# Revit family: VISS SQUARE LED LIGHT
name_source: partatom
category: Lighting Fixtures
units: mm (PartAtom-declared; Revit-internal decimal feet)

## family parameters
Cut with Voids When Loaded = No
Host = Face
Light Source = Yes
Part Type = Normal
Room Calculation Point = No
Round Connector Dimension = Use Diameter
Shared = No

## types (64) — shared parameters
Acoustic = Acoustic -130
Average life based on 77F(HRS) = 50000
B = 0' - 3 1/2"
CRI = 90
Color Filter = 16777215
Default Elevation = 0' - 0"
Description = The Viss Series has an unique square and round style with an LED light source illuminating its inner surface.
Dimming / Control = 0-10V
Dimming Lamp Color Temperature Shift = <None>
Fixture Height = 4' - 11"
IP Rating = 20
Load Classification = Lighting
Manufacturer = Above All Lighting
Power Factor = 1
Tilt Angle = -90.00°
Type Comments = VISS SQUARE LED LIGHT
URL = https://www.abovealllighting.com
Voltage = 120-277 V

## per-type parameters (varying)
| type | Acoustic Body | Aircraft Cable Pendant Mount | Apparent Load | B1 | B2 | Finish/Color | Fixture Width | H1 | Order number | Photometric Web File | Surface Acoustic Body | Surface Mount | Wattage Comments |
| VSI-S-1514-30901-ACPMK-WH | No | Yes | 19 VA | 0' - 6 19/32" | 0' - 3 3/32" | White | 1' - 2 3/16" | 4' - 11 3/32" | 17486 | generic | No | No | 15 W |
| VSI-S-2518-30901-ACPMK-WH | No | Yes | 31 VA | 0' - 8 11/32" | 0' - 4 27/32" | White | 1' - 5 11/16" | 4' - 11 3/16" | 17487 | generic | No | No | 25 W |
| VSI-S-3624-30901-ACPMK-WH | No | Yes | 31 VA | 0' - 11 5/16" | 0' - 7 13/16" | White | 1' - 11 19/32" | 4' - 11 1/2" | 17488 | generic | No | No | 36 W |
| VSI-S-5032-30901-ACPMK-WH | No | Yes | 63 VA | 1' - 3 1/4" | 0' - 11 3/4" | White | 2' - 7 1/2" | 5' - 0 5/32" | 17489 | generic | No | No | 50 W |
| VSI-S-1514-30901-ACPMK-BK | No | Yes | 19 VA | 0' - 6 19/32" | 0' - 3 3/32" | Black | 1' - 2 3/16" | 4' - 11 3/32" | 17490 | generic | No | No | 15 W |
| VSI-S-2518-30901-ACPMK-BK | No | Yes | 31 VA | 0' - 8 11/32" | 0' - 4 27/32" | Black | 1' - 5 11/16" | 4' - 11 3/16" | 17491 | generic | No | No | 25 W |
| VSI-S-3624-30901-ACPMK-BK | No | Yes | 31 VA | 0' - 11 5/16" | 0' - 7 13/16" | Black | 1' - 11 19/32" | 4' - 11 1/2" | 17492 | generic | No | No | 36 W |
| VSI-S-5032-30901-ACPMK-BK | No | Yes | 63 VA | 1' - 3 1/4" | 0' - 11 3/4" | Black | 2' - 7 1/2" | 5' - 0 5/32" | 17493 | generic | No | No | 50 W |
| VSI-S-1514-40901-ACPMK-WH | No | Yes | 19 VA | 0' - 6 19/32" | 0' - 3 3/32" | White | 1' - 2 3/16" | 4' - 11 3/32" | 17494 | generic | No | No | 15 W |
| VSI-S-2518-40901-ACPMK-WH | No | Yes | 31 VA | 0' - 8 11/32" | 0' - 4 27/32" | White | 1' - 5 11/16" | 4' - 11 3/16" | 17495 | generic | No | No | 25 W |
| VSI-S-3624-40901-ACPMK-WH | No | Yes | 31 VA | 0' - 11 5/16" | 0' - 7 13/16" | White | 1' - 11 19/32" | 4' - 11 1/2" | 17496 | VSI-S-3624-40901.IES | No | No | 36 W |
| VSI-S-5032-40901-ACPMK-WH | No | Yes | 63 VA | 1' - 3 1/4" | 0' - 11 3/4" | White | 2' - 7 1/2" | 5' - 0 5/32" | 17497 | VSI-S-5032-40901.IES | No | No | 50 W |
| VSI-S-1514-40901-ACPMK-BK | No | Yes | 19 VA | 0' - 6 19/32" | 0' - 3 3/32" | Black | 1' - 2 3/16" | 4' - 11 3/32" | 17498 | generic | No | No | 15 W |
| VSI-S-2518-40901-ACPMK-BK | No | Yes | 31 VA | 0' - 8 11/32" | 0' - 4 27/32" | Black | 1' - 5 11/16" | 4' - 11 3/16" | 17499 | generic | No | No | 25 W |
| VSI-S-3624-40901-ACPMK-BK | No | Yes | 31 VA | 0' - 11 5/16" | 0' - 7 13/16" | Black | 1' - 11 19/32" | 4' - 11 1/2" | 17500 | VSI-S-3624-40901.IES | No | No | 36 W |
| VSI-S-5032-40901-ACPMK-BK | No | Yes | 63 VA | 1' - 3 1/4" | 0' - 11 3/4" | Black | 2' - 7 1/2" | 5' - 0 5/32" | 17501 | VSI-S-5032-40901.IES | No | No | 50 W |
| VSI-S-LA-1514-30901-ACPMK-WH-NSAC-021 130 | Yes | Yes | 19 VA | 0' - 6 19/32" | 0' - 3 3/32" | White | 1' - 2 3/16" | 4' - 11 3/32" | 17502 | generic | No | No | 15 W |
| VSI-S-LA-2518-30901-ACPMK-WH-NSAC-021 130 | Yes | Yes | 31 VA | 0' - 8 11/32" | 0' - 4 27/32" | White | 1' - 5 11/16" | 4' - 11 3/16" | 17503 | generic | No | No | 25 W |
| VSI-S-LA-3624-30901-ACPMK-WH-NSAC-021 130 | Yes | Yes | 31 VA | 0' - 11 5/16" | 0' - 7 13/16" | White | 1' - 11 19/32" | 4' - 11 1/2" | 17504 | generic | No | No | 36 W |
| VSI-S-LA-5032-30901-ACPMK-WH-NSAC-021 130 | Yes | Yes | 63 VA | 1' - 3 1/4" | 0' - 11 3/4" | White | 2' - 7 1/2" | 5' - 0 5/32" | 17505 | generic | No | No | 50 W |
| VSI-S-LA-1514-30901-ACPMK-BK-NSAC-021 130 | Yes | Yes | 19 VA | 0' - 6 19/32" | 0' - 3 3/32" | Black | 1' - 2 3/16" | 4' - 11 3/32" | 17506 | generic | No | No | 15 W |
| VSI-S-LA-2518-30901-ACPMK-BK-NSAC-021 130 | Yes | Yes | 31 VA | 0' - 8 11/32" | 0' - 4 27/32" | Black | 1' - 5 11/16" | 4' - 11 3/16" | 17507 | generic | No | No | 25 W |
| VSI-S-LA-3624-30901-ACPMK-BK-NSAC-021 130 | Yes | Yes | 31 VA | 0' - 11 5/16" | 0' - 7 13/16" | Black | 1' - 11 19/32" | 4' - 11 1/2" | 17508 | generic | No | No | 36 W |
| VSI-S-LA-5032-30901-ACPMK-BK-NSAC-021 130 | Yes | Yes | 63 VA | 1' - 3 1/4" | 0' - 11 3/4" | Black | 2' - 7 1/2" | 5' - 0 5/32" | 17509 | generic | No | No | 50 W |
| VSI-S-LA-1514-40901-ACPMK-WH-NSAC-021 130 | Yes | Yes | 19 VA | 0' - 6 19/32" | 0' - 3 3/32" | White | 1' - 2 3/16" | 4' - 11 3/32" | 17510 | generic | No | No | 15 W |
| VSI-S-LA-2518-40901-ACPMK-WH-NSAC-021 130 | Yes | Yes | 31 VA | 0' - 8 11/32" | 0' - 4 27/32" | White | 1' - 5 11/16" | 4' - 11 3/16" | 17511 | generic | No | No | 25 W |
| VSI-S-LA-3624-40901-ACPMK-WH-NSAC-021 130 | Yes | Yes | 31 VA | 0' - 11 5/16" | 0' - 7 13/16" | White | 1' - 11 19/32" | 4' - 11 1/2" | 17512 | generic | No | No | 36 W |
| VSI-S-LA-5032-40901-ACPMK-WH-NSAC-021 130 | Yes | Yes | 63 VA | 1' - 3 1/4" | 0' - 11 3/4" | White | 2' - 7 1/2" | 5' - 0 5/32" | 17513 | generic | No | No | 50 W |
| VSI-S-LA-1514-40901-ACPMK-BK-NSAC-021 130 | Yes | Yes | 19 VA | 0' - 6 19/32" | 0' - 3 3/32" | Black | 1' - 2 3/16" | 4' - 11 3/32" | 17514 | generic | No | No | 15 W |
| VSI-S-LA-2518-40901-ACPMK-BK-NSAC-021 130 | Yes | Yes | 31 VA | 0' - 8 11/32" | 0' - 4 27/32" | Black | 1' - 5 11/16" | 4' - 11 3/16" | 17515 | generic | No | No | 25 W |
| VSI-S-LA-3624-40901-ACPMK-BK-NSAC-021 130 | Yes | Yes | 31 VA | 0' - 11 5/16" | 0' - 7 13/16" | Black | 1' - 11 19/32" | 4' - 11 1/2" | 17516 | generic | No | No | 36 W |
| VSI-S-LA-5032-40901-ACPMK-BK-NSAC-021 130 | Yes | Yes | 63 VA | 1' - 3 1/4" | 0' - 11 3/4" | Black | 2' - 7 1/2" | 5' - 0 5/32" | 17517 | generic | No | No | 50 W |
| VSI-S-1514-30901-SMK-WH | No | No | 19 VA | 0' - 6 19/32" | 0' - 3 3/32" | White | 1' - 2 3/16" | 4' - 11 3/32" | 17625 | generic | No | Yes | 15 W |
| VSI-S-2518-30901-SMK-WH | No | No | 31 VA | 0' - 8 11/32" | 0' - 4 27/32" | White | 1' - 5 11/16" | 4' - 11 3/16" | 17626 | generic | No | Yes | 25 W |
| VSI-S-3624-30901-SMK-WH | No | No | 31 VA | 0' - 11 5/16" | 0' - 7 13/16" | White | 1' - 11 19/32" | 4' - 11 1/2" | 17627 | generic | No | Yes | 36 W |
| VSI-S-5032-30901-SMK-WH | No | No | 63 VA | 1' - 3 1/4" | 0' - 11 3/4" | White | 2' - 7 1/2" | 5' - 0 5/32" | 17628 | generic | No | Yes | 50 W |
| VSI-S-1514-30901-SMK-BK | No | No | 19 VA | 0' - 6 19/32" | 0' - 3 3/32" | Black | 1' - 2 3/16" | 4' - 11 3/32" | 17629 | generic | No | Yes | 15 W |
| VSI-S-2518-30901-SMK-BK | No | No | 31 VA | 0' - 8 11/32" | 0' - 4 27/32" | Black | 1' - 5 11/16" | 4' - 11 3/16" | 17630 | generic | No | Yes | 25 W |
| VSI-S-3624-30901-SMK-BK | No | No | 31 VA | 0' - 11 5/16" | 0' - 7 13/16" | Black | 1' - 11 19/32" | 4' - 11 1/2" | 17631 | generic | No | Yes | 36 W |
| VSI-S-5032-30901-SMK-BK | No | No | 63 VA | 1' - 3 1/4" | 0' - 11 3/4" | Black | 2' - 7 1/2" | 5' - 0 5/32" | 17632 | generic | No | Yes | 50 W |
| VSI-S-1514-40901-SMK-WH | No | No | 19 VA | 0' - 6 19/32" | 0' - 3 3/32" | White | 1' - 2 3/16" | 4' - 11 3/32" | 17633 | generic | No | Yes | 15 W |
| VSI-S-2518-40901-SMK-WH | No | No | 31 VA | 0' - 8 11/32" | 0' - 4 27/32" | White | 1' - 5 11/16" | 4' - 11 3/16" | 17634 | generic | No | Yes | 25 W |
| VSI-S-3624-40901-SMK-WH | No | No | 31 VA | 0' - 11 5/16" | 0' - 7 13/16" | White | 1' - 11 19/32" | 4' - 11 1/2" | 17635 | VSI-S-3624-40901.IES | No | Yes | 36 W |
| VSI-S-5032-40901-SMK-WH | No | No | 63 VA | 1' - 3 1/4" | 0' - 11 3/4" | White | 2' - 7 1/2" | 5' - 0 5/32" | 17636 | VSI-S-5032-40901.IES | No | Yes | 50 W |
| VSI-S-1514-40901-SMK-BK | No | No | 19 VA | 0' - 6 19/32" | 0' - 3 3/32" | Black | 1' - 2 3/16" | 4' - 11 3/32" | 17637 | generic | No | Yes | 15 W |
| VSI-S-2518-40901-SMK-BK | No | No | 31 VA | 0' - 8 11/32" | 0' - 4 27/32" | Black | 1' - 5 11/16" | 4' - 11 3/16" | 17638 | generic | No | Yes | 25 W |
| VSI-S-3624-40901-SMK-BK | No | No | 31 VA | 0' - 11 5/16" | 0' - 7 13/16" | Black | 1' - 11 19/32" | 4' - 11 1/2" | 17639 | VSI-S-3624-40901.IES | No | Yes | 36 W |
| VSI-S-5032-40901-SMK-BK | No | No | 63 VA | 1' - 3 1/4" | 0' - 11 3/4" | Black | 2' - 7 1/2" | 5' - 0 5/32" | 17640 | VSI-S-5032-40901.IES | No | Yes | 50 W |
| VSI-S-LA-1514-30901-SMK-WH-NSAC-021 130 | No | No | 19 VA | 0' - 6 19/32" | 0' - 3 3/32" | White | 1' - 2 3/16" | 4' - 11 3/32" | 17641 | generic | Yes | Yes | 15 W |
| VSI-S-LA-2518-30901-SMK-WH-NSAC-021 130 | No | No | 31 VA | 0' - 8 11/32" | 0' - 4 27/32" | White | 1' - 5 11/16" | 4' - 11 3/16" | 17642 | generic | Yes | Yes | 25 W |
| VSI-S-LA-3624-30901-SMK-WH-NSAC-021 130 | No | No | 31 VA | 0' - 11 5/16" | 0' - 7 13/16" | White | 1' - 11 19/32" | 4' - 11 1/2" | 17643 | generic | Yes | Yes | 36 W |
| VSI-S-LA-5032-30901-SMK-WH-NSAC-021 130 | No | No | 63 VA | 1' - 3 1/4" | 0' - 11 3/4" | White | 2' - 7 1/2" | 5' - 0 5/32" | 17644 | generic | Yes | Yes | 50 W |
| VSI-S-LA-1514-30901-SMK-BK-NSAC-021 130 | No | No | 19 VA | 0' - 6 19/32" | 0' - 3 3/32" | Black | 1' - 2 3/16" | 4' - 11 3/32" | 17645 | generic | Yes | Yes | 15 W |
| VSI-S-LA-2518-30901-SMK-BK-NSAC-021 130 | No | No | 31 VA | 0' - 8 11/32" | 0' - 4 27/32" | Black | 1' - 5 11/16" | 4' - 11 3/16" | 17646 | generic | Yes | Yes | 25 W |
| VSI-S-LA-3624-30901-SMK-BK-NSAC-021 130 | No | No | 31 VA | 0' - 11 5/16" | 0' - 7 13/16" | Black | 1' - 11 19/32" | 4' - 11 1/2" | 17647 | generic | Yes | Yes | 36 W |
| VSI-S-LA-5032-30901-SMK-BK-NSAC-021 130 | No | No | 63 VA | 1' - 3 1/4" | 0' - 11 3/4" | Black | 2' - 7 1/2" | 5' - 0 5/32" | 17648 | generic | Yes | Yes | 50 W |
| VSI-S-LA-1514-40901-SMK-WH-NSAC-021 130 | No | No | 19 VA | 0' - 6 19/32" | 0' - 3 3/32" | White | 1' - 2 3/16" | 4' - 11 3/32" | 17649 | generic | Yes | Yes | 15 W |
| VSI-S-LA-1514-40901-SMK-BK-NSAC-021 130 | No | No | 19 VA | 0' - 6 19/32" | 0' - 3 3/32" | Black | 1' - 2 3/16" | 4' - 11 3/32" | 17653 | generic | Yes | Yes | 15 W |
| VSI-S-LA-2518-40901-SMK-WH-NSAC-021 130 | No | No | 31 VA | 0' - 8 11/32" | 0' - 4 27/32" | White | 1' - 5 11/16" | 4' - 11 3/16" | 17650 | generic | Yes | Yes | 25 W |
| VSI-S-LA-2518-40901-SMK-BK-NSAC-021 130 | No | No | 31 VA | 0' - 8 11/32" | 0' - 4 27/32" | Black | 1' - 5 11/16" | 4' - 11 3/16" | 17654 | generic | Yes | Yes | 25 W |
| VSI-S-LA-3624-40901-SMK-WH-NSAC-021 130 | No | No | 31 VA | 0' - 11 5/16" | 0' - 7 13/16" | White | 1' - 11 19/32" | 4' - 11 1/2" | 17651 | generic | Yes | Yes | 36 W |
| VSI-S-LA-5032-40901-SMK-WH-NSAC-021 130 | No | No | 63 VA | 1' - 3 1/4" | 0' - 11 3/4" | White | 2' - 7 1/2" | 5' - 0 5/32" | 17652 | generic | Yes | Yes | 50 W |
| VSI-S-LA-3624-40901-SMK-BK-NSAC-021 130 | No | No | 31 VA | 0' - 11 5/16" | 0' - 7 13/16" | Black | 1' - 11 19/32" | 4' - 11 1/2" | 17655 | generic | Yes | Yes | 36 W |
| VSI-S-LA-5032-40901-SMK-BK-NSAC-021 130 | No | No | 63 VA | 1' - 3 1/4" | 0' - 11 3/4" | Black | 2' - 7 1/2" | 5' - 0 5/32" | 17656 | generic | Yes | Yes | 50 W |

note: column(s) folded — value = type name in every type: Model

## geometry (parser evidence)
native form markers: Sweep x5
no freeform markers — native parametric forms only
